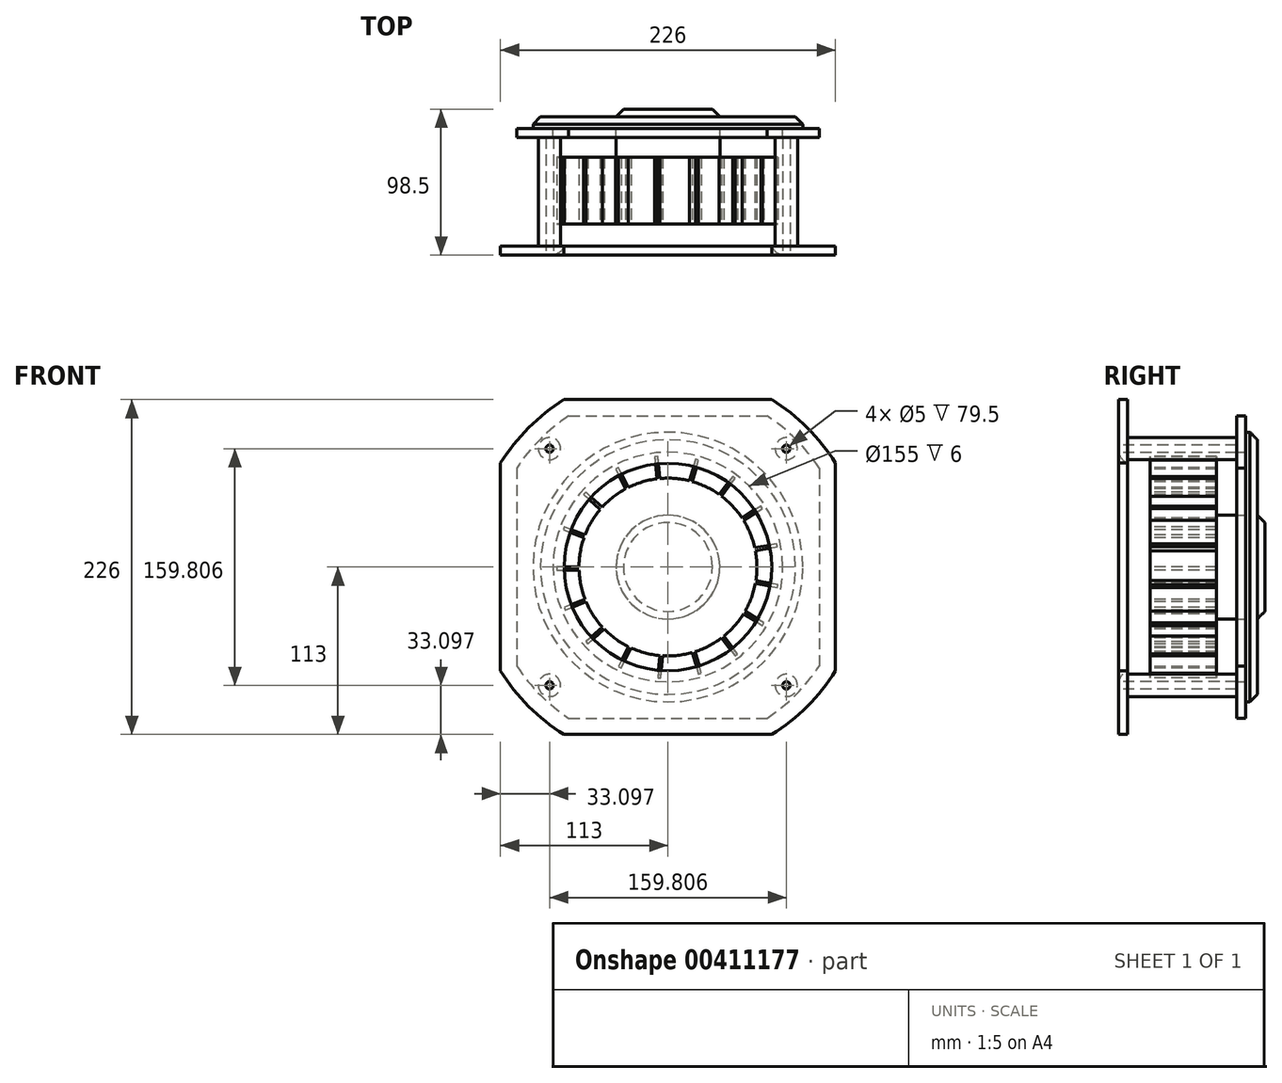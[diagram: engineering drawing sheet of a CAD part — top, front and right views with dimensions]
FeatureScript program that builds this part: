
annotation { "Feature Type Name" : "Feature", "Feature Type Description" : "" }
export const myFeature = defineFeature(function(context is Context, id is Id, definition is map)
    precondition{}
    {
        {
            var Q0;
            Q0=qCreatedBy(makeId("Front.planeOp"),FACE);
            var sketch = newSketch(context, id + "F0", { "sketchPlane" : qUnion([Q0])});
            skLineSegment(sketch, "E0", {"start": v(-187.98, 0) * mm, "end": v(190.84, 0) * mm, "construction": true});
            skLineSegment(sketch, "E1", {"start": v(0, 189.41) * mm, "end": v(0, -189.41) * mm, "construction": true});
            skLineSegment(sketch, "E2", {"start": v(-139.8, 139.8) * mm, "end": v(0, 0) * mm, "construction": true});
            skCircle(sketch, "E3", {"center": v(0, 0) * mm, "radius": 113 * mm, "construction": true});
            skLineSegment(sketch, "E4.bottom", {"start": v(-113, 113) * mm, "end": v(-70.14, 113) * mm, "construction": true});
            skLineSegment(sketch, "E4.top", {"start": v(-113, -113) * mm, "end": v(-70.14, -113) * mm, "construction": true});
            skLineSegment(sketch, "E4.left", {"start": v(-113, 113) * mm, "end": v(-113, 70.14) * mm, "construction": true});
            skLineSegment(sketch, "E4.right", {"start": v(113, 113) * mm, "end": v(113, 70.14) * mm, "construction": true});
            skLineSegment(sketch, "E5", {"start": v(-113, 70.14) * mm, "end": v(-113, 70.14) * mm});
            skArc(sketch, "E6", {"start": v(-70.14, 113) * mm, "mid": v(-94.05, 94.05) * mm, "end": v(-113, 70.14) * mm});
            skArc(sketch, "E7", {"start": v(70.14, 113) * mm, "mid": v(0, 133) * mm, "end": v(-70.14, 113) * mm, "construction": true});
            skArc(sketch, "E8", {"start": v(70.14, -113) * mm, "mid": v(94.05, -94.05) * mm, "end": v(113, -70.14) * mm});
            skArc(sketch, "E9", {"start": v(113, -70.14) * mm, "mid": v(133, 0) * mm, "end": v(113, 70.14) * mm, "construction": true});
            skLineSegment(sketch, "E10", {"start": v(113, -70.14) * mm, "end": v(113, -113) * mm, "construction": true});
            skLineSegment(sketch, "E11", {"start": v(113, 70.14) * mm, "end": v(113, -70.14) * mm});
            skArc(sketch, "E12", {"start": v(113, 70.14) * mm, "mid": v(94.05, 94.05) * mm, "end": v(70.14, 113) * mm});
            skLineSegment(sketch, "E13", {"start": v(70.14, 113) * mm, "end": v(113, 113) * mm, "construction": true});
            skLineSegment(sketch, "E14", {"start": v(-70.14, 113) * mm, "end": v(70.14, 113) * mm});
            skArc(sketch, "E15", {"start": v(-113, 70.14) * mm, "mid": v(-133, 0) * mm, "end": v(-113, -70.14) * mm, "construction": true});
            skLineSegment(sketch, "E16", {"start": v(-113, 70.14) * mm, "end": v(-113, -70.47) * mm});
            skArc(sketch, "E17", {"start": v(-113, -70.14) * mm, "mid": v(-94.05, -94.05) * mm, "end": v(-70.14, -113) * mm});
            skLineSegment(sketch, "E18", {"start": v(-113, -70.47) * mm, "end": v(-113, -113) * mm, "construction": true});
            skLineSegment(sketch, "E19", {"start": v(70.14, -113) * mm, "end": v(70.14, -113) * mm});
            skLineSegment(sketch, "E20", {"start": v(70.14, -113) * mm, "end": v(113, -113) * mm, "construction": true});
            skArc(sketch, "E21", {"start": v(-70.14, -113) * mm, "mid": v(0, -133) * mm, "end": v(70.14, -113) * mm, "construction": true});
            skLineSegment(sketch, "E22", {"start": v(-70.14, -113) * mm, "end": v(-70.14, -113) * mm});
            skLineSegment(sketch, "E23", {"start": v(-70.14, -113) * mm, "end": v(70.14, -113) * mm});
            skCircle(sketch, "E24", {"center": v(-79.9, 79.9) * mm, "radius": 2.5 * mm});
            skCircle(sketch, "E25.1.0", {"center": v(-79.9, -79.9) * mm, "radius": 2.5 * mm});
            skCircle(sketch, "E25.2.0", {"center": v(79.9, -79.9) * mm, "radius": 2.5 * mm});
            skCircle(sketch, "E25.3.0", {"center": v(79.9, 79.9) * mm, "radius": 2.5 * mm});
            skCircle(sketch, "E26", {"center": v(0, 0) * mm, "radius": 70 * mm});
            skSolve(sketch);
        }
        {
            var Q0;
            {var subQ2=sQuery(id+"F0.wireOp",EDGE,"E6");Q0=makeQuery(id+"F0.imprint","IMPRINT",FACE,{"disambiguationData":[TD([[makeQuery(id+"F0.imprint","IMPRINT",EDGE,{"derivedFrom":subQ2}),1.0]])]});}
            extrude(context, id + "F1", {"entities" : qUnion([Q0]), "depth" : -6 * mm});
        }
        {
            var Q0;
            Q0=makeQuery(id+"F1.opExtrude","CAP_FACE",FACE,{"disambiguationData":[OSD([sQuery(id+"F0.wireOp",EDGE,"E6"),sQuery(id+"F0.wireOp",EDGE,"E8"),sQuery(id+"F0.wireOp",EDGE,"E11"),sQuery(id+"F0.wireOp",EDGE,"E12"),sQuery(id+"F0.wireOp",EDGE,"E14"),sQuery(id+"F0.wireOp",EDGE,"E16"),sQuery(id+"F0.wireOp",EDGE,"E17"),sQuery(id+"F0.wireOp",EDGE,"E23"),sQuery(id+"F0.wireOp",EDGE,"E24"),sQuery(id+"F0.wireOp",EDGE,"E25.1.0"),sQuery(id+"F0.wireOp",EDGE,"E25.2.0"),sQuery(id+"F0.wireOp",EDGE,"E25.3.0"),sQuery(id+"F0.wireOp",EDGE,"E26")])],"isStart":false});
            cPlane(context, id + "F2", {"entities" : qUnion([Q0]), "cplaneType" : CPlaneType.OFFSET, "offset" : 79.5 * mm, "width" : 150 * mm, "height" : 150 * mm});
        }
        {
            var Q0;
            Q0=qCreatedBy(id+"F2.planeOp",FACE);
            var sketch = newSketch(context, id + "F3", { "sketchPlane" : qUnion([Q0])});
            skLineSegment(sketch, "E27.bottom", {"start": v(102, 102) * mm, "end": v(66.93, 102) * mm, "construction": true});
            skLineSegment(sketch, "E27.top", {"start": v(102, -102) * mm, "end": v(66.93, -102) * mm, "construction": true});
            skLineSegment(sketch, "E27.left", {"start": v(102, 102) * mm, "end": v(102, 66.93) * mm, "construction": true});
            skLineSegment(sketch, "E27.right", {"start": v(-102, 102) * mm, "end": v(-102, 66.93) * mm, "construction": true});
            skCircle(sketch, "E28", {"center": v(0, 0) * mm, "radius": 102 * mm, "construction": true});
            skLineSegment(sketch, "E29", {"start": v(102, 66.93) * mm, "end": v(102, -66.93) * mm});
            skLineSegment(sketch, "E30", {"start": v(102, 66.93) * mm, "end": v(102, 66.93) * mm});
            skLineSegment(sketch, "E31", {"start": v(66.93, 102) * mm, "end": v(-66.93, 102) * mm});
            skArc(sketch, "E32", {"start": v(66.93, 102) * mm, "mid": v(0, 122) * mm, "end": v(-66.93, 102) * mm, "construction": true});
            skArc(sketch, "E33", {"start": v(102, 66.93) * mm, "mid": v(86.27, 86.27) * mm, "end": v(66.93, 102) * mm});
            skArc(sketch, "E34", {"start": v(-66.93, 102) * mm, "mid": v(-86.27, 86.27) * mm, "end": v(-102, 66.93) * mm});
            skLineSegment(sketch, "E35", {"start": v(-66.93, 102) * mm, "end": v(-102, 102) * mm, "construction": true});
            skArc(sketch, "E36", {"start": v(-102, 66.93) * mm, "mid": v(-122, 0) * mm, "end": v(-102, -66.93) * mm, "construction": true});
            skLineSegment(sketch, "E37", {"start": v(-102, 66.93) * mm, "end": v(-102, -66.93) * mm});
            skLineSegment(sketch, "E38", {"start": v(-102, -66.93) * mm, "end": v(-102, -102) * mm, "construction": true});
            skArc(sketch, "E39", {"start": v(-102, -66.93) * mm, "mid": v(-86.27, -86.27) * mm, "end": v(-66.93, -102) * mm});
            skLineSegment(sketch, "E40", {"start": v(-66.93, -102) * mm, "end": v(-102, -102) * mm, "construction": true});
            skArc(sketch, "E41", {"start": v(-66.93, -102) * mm, "mid": v(0, -122) * mm, "end": v(66.93, -102) * mm, "construction": true});
            skArc(sketch, "E42", {"start": v(66.93, -102) * mm, "mid": v(86.27, -86.27) * mm, "end": v(102, -66.93) * mm});
            skLineSegment(sketch, "E43", {"start": v(66.93, -102) * mm, "end": v(-66.93, -102) * mm});
            skLineSegment(sketch, "E44", {"start": v(102, -66.93) * mm, "end": v(102, -102) * mm, "construction": true});
            skArc(sketch, "E45", {"start": v(102, -66.93) * mm, "mid": v(122, 0) * mm, "end": v(102, 66.93) * mm, "construction": true});
            skCircle(sketch, "E46", {"center": v(0, 0) * mm, "radius": 77.5 * mm});
            skSolve(sketch);
        }
        {
            var Q0;
            Q0=makeQuery(id+"F3.imprint","IMPRINT",FACE,{"disambiguationData":[TD([[makeQuery(id+"F3.imprint","IMPRINT",EDGE,{"derivedFrom":sQuery(id+"F3.wireOp",EDGE,"E29")}),-1.0]])]});
            extrude(context, id + "F4", {"entities" : qUnion([Q0]), "oppositeDirection" : true, "depth" : 6 * mm});
        }
        {
            var Q0;
            Q0=makeQuery(id+"F1.opExtrude","CAP_FACE",FACE,{"disambiguationData":[OSD([sQuery(id+"F0.wireOp",EDGE,"E6"),sQuery(id+"F0.wireOp",EDGE,"E8"),sQuery(id+"F0.wireOp",EDGE,"E11"),sQuery(id+"F0.wireOp",EDGE,"E12"),sQuery(id+"F0.wireOp",EDGE,"E14"),sQuery(id+"F0.wireOp",EDGE,"E16"),sQuery(id+"F0.wireOp",EDGE,"E17"),sQuery(id+"F0.wireOp",EDGE,"E23"),sQuery(id+"F0.wireOp",EDGE,"E24"),sQuery(id+"F0.wireOp",EDGE,"E25.1.0"),sQuery(id+"F0.wireOp",EDGE,"E25.2.0"),sQuery(id+"F0.wireOp",EDGE,"E25.3.0"),sQuery(id+"F0.wireOp",EDGE,"E26")])],"isStart":false});
            var sketch = newSketch(context, id + "F5", { "sketchPlane" : qUnion([Q0])});
            skLineSegment(sketch, "E47.0.0", {"start": v(-113, 70.14) * mm, "end": v(-113, -70.14) * mm, "construction": true});
            skArc(sketch, "E47.0.1", {"start": v(-113, -70.14) * mm, "mid": v(-94.05, -94.05) * mm, "end": v(-70.14, -113) * mm, "construction": true});
            skLineSegment(sketch, "E47.0.2", {"start": v(-70.14, -113) * mm, "end": v(70.14, -113) * mm, "construction": true});
            skArc(sketch, "E47.0.3", {"start": v(70.14, -113) * mm, "mid": v(94.05, -94.05) * mm, "end": v(113, -70.14) * mm, "construction": true});
            skLineSegment(sketch, "E47.0.4", {"start": v(113, -70.14) * mm, "end": v(113, 70.14) * mm, "construction": true});
            skArc(sketch, "E47.0.5", {"start": v(113, 70.14) * mm, "mid": v(94.05, 94.05) * mm, "end": v(70.14, 113) * mm, "construction": true});
            skLineSegment(sketch, "E47.0.6", {"start": v(70.14, 113) * mm, "end": v(-70.14, 113) * mm, "construction": true});
            skArc(sketch, "E47.0.7", {"start": v(-70.14, 113) * mm, "mid": v(-94.05, 94.05) * mm, "end": v(-113, 70.14) * mm, "construction": true});
            skCircle(sketch, "E48.0", {"center": v(79.9, 79.9) * mm, "radius": 2.5 * mm});
            skCircle(sketch, "E49.0", {"center": v(-79.9, 79.9) * mm, "radius": 2.5 * mm});
            skCircle(sketch, "E50.0", {"center": v(79.9, -79.9) * mm, "radius": 2.5 * mm});
            skCircle(sketch, "E51.0", {"center": v(-79.9, -79.9) * mm, "radius": 2.5 * mm});
            skCircle(sketch, "E52.0", {"center": v(0, 0) * mm, "radius": 70 * mm, "construction": true});
            skCircle(sketch, "E53.0", {"center": v(-79.9, 79.9) * mm, "radius": 7.5 * mm});
            skCircle(sketch, "E54.0", {"center": v(79.9, 79.9) * mm, "radius": 7.5 * mm});
            skCircle(sketch, "E55.0", {"center": v(-79.9, -79.9) * mm, "radius": 7.5 * mm});
            skCircle(sketch, "E56.0", {"center": v(79.9, -79.9) * mm, "radius": 7.5 * mm});
            skSolve(sketch);
        }
        {
            var Q0;
            Q0=makeQuery(id+"F5.imprint","IMPRINT",FACE,{"disambiguationData":[TD([[makeQuery(id+"F5.imprint","IMPRINT",EDGE,{"derivedFrom":sQuery(id+"F5.wireOp",EDGE,"E49.0")}),1.0]])]});
            var Q1;
            Q1=makeQuery(id+"F5.imprint","IMPRINT",FACE,{"disambiguationData":[TD([[makeQuery(id+"F5.imprint","IMPRINT",EDGE,{"derivedFrom":sQuery(id+"F5.wireOp",EDGE,"E48.0")}),1.0]])]});
            var Q2;
            Q2=makeQuery(id+"F5.imprint","IMPRINT",FACE,{"disambiguationData":[TD([[makeQuery(id+"F5.imprint","IMPRINT",EDGE,{"derivedFrom":sQuery(id+"F5.wireOp",EDGE,"E50.0")}),1.0]])]});
            var Q3;
            Q3=makeQuery(id+"F5.imprint","IMPRINT",FACE,{"disambiguationData":[TD([[makeQuery(id+"F5.imprint","IMPRINT",EDGE,{"derivedFrom":sQuery(id+"F5.wireOp",EDGE,"E51.0")}),1.0]])]});
            extrude(context, id + "F6", {"entities" : qUnion([Q0, Q1, Q2, Q3]), "operationType" : NewBodyOperationType.ADD, "endBound" : BoundingType.UP_TO_NEXT, "depth" : 25 * mm});
        }
        {
            var Q0;
            Q0=makeQuery(id+"F1.opExtrude","CAP_FACE",FACE,{"disambiguationData":[OSD([sQuery(id+"F0.wireOp",EDGE,"E6"),sQuery(id+"F0.wireOp",EDGE,"E8"),sQuery(id+"F0.wireOp",EDGE,"E11"),sQuery(id+"F0.wireOp",EDGE,"E12"),sQuery(id+"F0.wireOp",EDGE,"E14"),sQuery(id+"F0.wireOp",EDGE,"E16"),sQuery(id+"F0.wireOp",EDGE,"E17"),sQuery(id+"F0.wireOp",EDGE,"E23"),sQuery(id+"F0.wireOp",EDGE,"E24"),sQuery(id+"F0.wireOp",EDGE,"E25.1.0"),sQuery(id+"F0.wireOp",EDGE,"E25.2.0"),sQuery(id+"F0.wireOp",EDGE,"E25.3.0"),sQuery(id+"F0.wireOp",EDGE,"E26")])],"isStart":false});
            cPlane(context, id + "F7", {"entities" : qUnion([Q0]), "cplaneType" : CPlaneType.OFFSET, "offset" : 15 * mm, "width" : 150 * mm, "height" : 150 * mm});
        }
        {
            var Q0;
            Q0=qCreatedBy(id+"F7.planeOp",FACE);
            var sketch = newSketch(context, id + "F8", { "sketchPlane" : qUnion([Q0])});
            skCircle(sketch, "E57.0", {"center": v(0, 0) * mm, "radius": 70 * mm, "construction": true});
            skCircle(sketch, "E58.0", {"center": v(0, 0) * mm, "radius": 60 * mm});
            skLineSegment(sketch, "E59", {"start": v(60, 0) * mm, "end": v(75, 0) * mm});
            skLineSegment(sketch, "E60", {"start": v(75, 0) * mm, "end": v(75, -2) * mm});
            skLineSegment(sketch, "E61", {"start": v(75, -2) * mm, "end": v(59.97, -2) * mm});
            skLineSegment(sketch, "E62", {"start": v(59.97, -2) * mm, "end": v(60, 0) * mm});
            skLineSegment(sketch, "E63.1.0", {"start": v(55.95, 21.67) * mm, "end": v(69.94, 27.1) * mm});
            skLineSegment(sketch, "E63.1.1", {"start": v(70.66, 25.23) * mm, "end": v(56.64, 19.8) * mm});
            skLineSegment(sketch, "E63.1.2", {"start": v(69.94, 27.1) * mm, "end": v(70.66, 25.23) * mm});
            skLineSegment(sketch, "E63.2.0", {"start": v(44.34, 40.42) * mm, "end": v(55.43, 50.53) * mm});
            skLineSegment(sketch, "E63.2.1", {"start": v(56.77, 49.05) * mm, "end": v(45.66, 38.92) * mm});
            skLineSegment(sketch, "E63.2.2", {"start": v(55.43, 50.53) * mm, "end": v(56.77, 49.05) * mm});
            skLineSegment(sketch, "E63.3.0", {"start": v(26.74, 53.7) * mm, "end": v(33.43, 67.14) * mm});
            skLineSegment(sketch, "E63.3.1", {"start": v(35.22, 66.25) * mm, "end": v(28.52, 52.79) * mm});
            skLineSegment(sketch, "E63.3.2", {"start": v(33.43, 67.14) * mm, "end": v(35.22, 66.25) * mm});
            skLineSegment(sketch, "E63.4.0", {"start": v(5.54, 59.74) * mm, "end": v(6.92, 74.68) * mm});
            skLineSegment(sketch, "E63.4.1", {"start": v(8.91, 74.5) * mm, "end": v(7.52, 59.53) * mm});
            skLineSegment(sketch, "E63.4.2", {"start": v(6.92, 74.68) * mm, "end": v(8.91, 74.5) * mm});
            skLineSegment(sketch, "E63.5.0", {"start": v(-16.42, 57.7) * mm, "end": v(-20.52, 72.14) * mm});
            skLineSegment(sketch, "E63.5.1", {"start": v(-18.6, 72.68) * mm, "end": v(-14.49, 58.22) * mm});
            skLineSegment(sketch, "E63.5.2", {"start": v(-20.52, 72.14) * mm, "end": v(-18.6, 72.68) * mm});
            skLineSegment(sketch, "E63.6.0", {"start": v(-36.16, 47.88) * mm, "end": v(-45.2, 59.85) * mm});
            skLineSegment(sketch, "E63.6.1", {"start": v(-43.6, 61.06) * mm, "end": v(-34.54, 49.06) * mm});
            skLineSegment(sketch, "E63.6.2", {"start": v(-45.2, 59.85) * mm, "end": v(-43.6, 61.06) * mm});
            skLineSegment(sketch, "E63.7.0", {"start": v(-51.01, 31.59) * mm, "end": v(-63.77, 39.48) * mm});
            skLineSegment(sketch, "E63.7.1", {"start": v(-62.71, 41.18) * mm, "end": v(-49.93, 33.27) * mm});
            skLineSegment(sketch, "E63.7.2", {"start": v(-63.77, 39.48) * mm, "end": v(-62.71, 41.18) * mm});
            skLineSegment(sketch, "E63.8.0", {"start": v(-58.98, 11.02) * mm, "end": v(-73.72, 13.78) * mm});
            skLineSegment(sketch, "E63.8.1", {"start": v(-73.36, 15.75) * mm, "end": v(-58.58, 12.98) * mm});
            skLineSegment(sketch, "E63.8.2", {"start": v(-73.72, 13.78) * mm, "end": v(-73.36, 15.75) * mm});
            skLineSegment(sketch, "E63.9.0", {"start": v(-58.98, -11.02) * mm, "end": v(-73.72, -13.78) * mm});
            skLineSegment(sketch, "E63.9.1", {"start": v(-74.1, -11.82) * mm, "end": v(-59.31, -9.05) * mm});
            skLineSegment(sketch, "E63.9.2", {"start": v(-73.72, -13.78) * mm, "end": v(-74.1, -11.82) * mm});
            skLineSegment(sketch, "E63.10.0", {"start": v(-51.01, -31.59) * mm, "end": v(-63.77, -39.48) * mm});
            skLineSegment(sketch, "E63.10.1", {"start": v(-64.82, -37.78) * mm, "end": v(-52.04, -29.87) * mm});
            skLineSegment(sketch, "E63.10.2", {"start": v(-63.77, -39.48) * mm, "end": v(-64.82, -37.78) * mm});
            skLineSegment(sketch, "E63.11.0", {"start": v(-36.16, -47.88) * mm, "end": v(-45.2, -59.85) * mm});
            skLineSegment(sketch, "E63.11.1", {"start": v(-46.8, -58.65) * mm, "end": v(-37.73, -46.65) * mm});
            skLineSegment(sketch, "E63.11.2", {"start": v(-45.2, -59.85) * mm, "end": v(-46.8, -58.65) * mm});
            skLineSegment(sketch, "E63.12.0", {"start": v(-16.42, -57.7) * mm, "end": v(-20.52, -72.14) * mm});
            skLineSegment(sketch, "E63.12.1", {"start": v(-22.45, -71.59) * mm, "end": v(-18.33, -57.13) * mm});
            skLineSegment(sketch, "E63.12.2", {"start": v(-20.52, -72.14) * mm, "end": v(-22.45, -71.59) * mm});
            skLineSegment(sketch, "E63.13.0", {"start": v(5.54, -59.74) * mm, "end": v(6.92, -74.68) * mm});
            skLineSegment(sketch, "E63.13.1", {"start": v(4.93, -74.86) * mm, "end": v(3.54, -59.9) * mm});
            skLineSegment(sketch, "E63.13.2", {"start": v(6.92, -74.68) * mm, "end": v(4.93, -74.86) * mm});
            skLineSegment(sketch, "E63.14.0", {"start": v(26.74, -53.7) * mm, "end": v(33.43, -67.14) * mm});
            skLineSegment(sketch, "E63.14.1", {"start": v(31.64, -68.03) * mm, "end": v(24.94, -54.57) * mm});
            skLineSegment(sketch, "E63.14.2", {"start": v(33.43, -67.14) * mm, "end": v(31.64, -68.03) * mm});
            skLineSegment(sketch, "E63.15.0", {"start": v(44.34, -40.42) * mm, "end": v(55.43, -50.53) * mm});
            skLineSegment(sketch, "E63.15.1", {"start": v(54.08, -52) * mm, "end": v(42.97, -41.88) * mm});
            skLineSegment(sketch, "E63.15.2", {"start": v(55.43, -50.53) * mm, "end": v(54.08, -52) * mm});
            skLineSegment(sketch, "E63.16.0", {"start": v(55.95, -21.67) * mm, "end": v(69.94, -27.1) * mm});
            skLineSegment(sketch, "E63.16.1", {"start": v(69.21, -28.96) * mm, "end": v(55.2, -23.53) * mm});
            skLineSegment(sketch, "E63.16.2", {"start": v(69.94, -27.1) * mm, "end": v(69.21, -28.96) * mm});
            skSolve(sketch);
        }
        {
            var Q0;
            Q0=qSketchRegion(id+"F8",true);
            extrude(context, id + "F9", {"entities" : qUnion([Q0]), "operationType" : NewBodyOperationType.ADD, "depth" : 45 * mm});
        }
        {
            var Q0;
            Q0=makeQuery(id+"F1.opExtrude","CAP_FACE",FACE,{"disambiguationData":[OSD([sQuery(id+"F0.wireOp",EDGE,"E6"),sQuery(id+"F0.wireOp",EDGE,"E8"),sQuery(id+"F0.wireOp",EDGE,"E11"),sQuery(id+"F0.wireOp",EDGE,"E12"),sQuery(id+"F0.wireOp",EDGE,"E14"),sQuery(id+"F0.wireOp",EDGE,"E16"),sQuery(id+"F0.wireOp",EDGE,"E17"),sQuery(id+"F0.wireOp",EDGE,"E23"),sQuery(id+"F0.wireOp",EDGE,"E24"),sQuery(id+"F0.wireOp",EDGE,"E25.1.0"),sQuery(id+"F0.wireOp",EDGE,"E25.2.0"),sQuery(id+"F0.wireOp",EDGE,"E25.3.0"),sQuery(id+"F0.wireOp",EDGE,"E26")])],"isStart":true});
            cPlane(context, id + "F10", {"entities" : qUnion([Q0]), "cplaneType" : CPlaneType.OFFSET, "offset" : 98.5 * mm, "oppositeDirection" : true, "width" : 150 * mm, "height" : 150 * mm});
        }
        {
            var Q0;
            Q0=qCreatedBy(id+"F10.planeOp",FACE);
            var sketch = newSketch(context, id + "F11", { "sketchPlane" : qUnion([Q0])});
            skCircle(sketch, "E64", {"center": v(0, 0) * mm, "radius": 35 * mm});
            skCircle(sketch, "E65", {"center": v(0, 0) * mm, "radius": 85 * mm});
            skCircle(sketch, "E66", {"center": v(0, 0) * mm, "radius": 55 * mm});
            skSolve(sketch);
        }
        {
            var Q0;
            Q0=makeQuery(id+"F11.imprint","IMPRINT",FACE,{"disambiguationData":[TD([[makeQuery(id+"F11.imprint","IMPRINT",EDGE,{"derivedFrom":sQuery(id+"F11.wireOp",EDGE,"E64")}),1.0]])]});
            extrude(context, id + "F12", {"entities" : qUnion([Q0]), "operationType" : NewBodyOperationType.ADD, "endBound" : BoundingType.UP_TO_NEXT, "depth" : 25 * mm});
        }
        {
            var Q0;
            Q0=makeQuery(id+"F4.opExtrude","CAP_FACE",FACE,{"disambiguationData":[OSD([sQuery(id+"F3.wireOp",EDGE,"E29"),sQuery(id+"F3.wireOp",EDGE,"E31"),sQuery(id+"F3.wireOp",EDGE,"E33"),sQuery(id+"F3.wireOp",EDGE,"E34"),sQuery(id+"F3.wireOp",EDGE,"E37"),sQuery(id+"F3.wireOp",EDGE,"E39"),sQuery(id+"F3.wireOp",EDGE,"E42"),sQuery(id+"F3.wireOp",EDGE,"E43"),sQuery(id+"F3.wireOp",EDGE,"E46")])],"isStart":true});
            var sketch = newSketch(context, id + "F13", { "sketchPlane" : qUnion([Q0])});
            skCircle(sketch, "E67", {"center": v(0, 0) * mm, "radius": 91.02 * mm});
            skCircle(sketch, "E68", {"center": v(0, 0) * mm, "radius": 34.98 * mm});
            skSolve(sketch);
        }
        {
            var Q0;
            Q0=qSketchRegion(id+"F13",true);
            extrude(context, id + "F14", {"entities" : qUnion([Q0]), "operationType" : NewBodyOperationType.ADD, "depth" : 8 * mm});
        }
        {
            var Q0;
            Q0=makeQuery(id+"F14.opExtrude","CAP_EDGE",EDGE,{"disambiguationData":[OSD([sQuery(id+"F13.wireOp",EDGE,"E67")])],"isStart":false});
            var Q1;
            Q1=makeQuery(id+"F12.opExtrude","CAP_EDGE",EDGE,{"disambiguationData":[OSD([sQuery(id+"F11.wireOp",EDGE,"E64")])],"isStart":true});
            chamfer(context, id + "F15", {"entities" : qUnion([Q0, Q1]), "width" : 5 * mm, "tangentPropagation" : true});
        }
        {
            var Q0;
            Q0=makeQuery(id+"F1.opExtrude","CAP_EDGE",EDGE,{"disambiguationData":[OSD([sQuery(id+"F0.wireOp",EDGE,"E26")])],"isStart":true});
            fillet(context, id + "F16", {"entities" : qUnion([Q0]), "radius" : 10 * mm, "tangentPropagation" : true, "allowEdgeOverflow" : false});
        }
        {
            var Q0;
            Q0=makeQuery(id+"F13.imprint","IMPRINT",FACE,{"disambiguationData":[TD([[makeQuery(id+"F13.imprint","IMPRINT",EDGE,{"derivedFrom":sQuery(id+"F13.wireOp",EDGE,"E67")}),1.0]])]});
            var Q1;
            Q1=makeQuery(id+"F13.imprint","IMPRINT",FACE,{"disambiguationData":[TD([[makeQuery(id+"F13.imprint","IMPRINT",EDGE,{"derivedFrom":sQuery(id+"F13.wireOp",EDGE,"E68")}),-1.0]])]});
            extrude(context, id + "F17", {"entities" : qUnion([Q0, Q1]), "depth" : 25 * mm});
        }
        {
            var Q0;
            Q0=makeQuery(id+"F17.opExtrude","SWEPT_BODY",BODY,{"disambiguationData":[OSD([sQuery(id+"F13.wireOp",EDGE,"E67"),sQuery(id+"F13.wireOp",EDGE,"E68")])]});
            deleteBodies(context, id + "F18", {"entities" : qUnion([Q0])});
        }
    });
